FCSTD DOCUMENT  (FreeCAD 0.19R24291 (Git))
Label: curve_test
License: All rights reserved
LicenseURL: http://en.wikipedia.org/wiki/All_rights_reserved
objects: Sketcher::SketchObject×2, PartDesign::Body×1
note: 3 computed .brp shape members not serialized (recipe doc carries the construction recipe); baked Part::Feature solids carry a one-line shape summary decoded from their .brp

FEATURE [Sketcher::SketchObject] Sketch
  FullyConstrained = false
  MapMode = 5
  Placement = pos=(0,0,0) rot=(1,0,0;1.5708rad)
  Support = -> [XZ_Plane]
  sketch-geometry (15):
    g0-g4: Circle x5 (B-spline internal-alignment scaffolding for g5; pole/knot coordinates omitted)
    g5: BSplineCurve PolesCount=5 KnotsCount=3 Degree=3 IsPeriodic=0
    g6: GeomPoint X=-25.4415 Y=43.3775 Z=0
    g7: GeomPoint X=-23.7858 Y=19.2881 Z=0
    g8: GeomPoint X=-22.2406 Y=0 Z=0
    g9: Circle CenterX=-7.83243 CenterY=0 CenterZ=0 NormalX=0 NormalY=0 NormalZ=1 AngleXU=0 Radius=1
    g10: Circle CenterX=1.51501 CenterY=20.0593 CenterZ=0 NormalX=0 NormalY=0 NormalZ=1 AngleXU=0 Radius=1
    g11: Circle CenterX=-8.09944 CenterY=43.783 CenterZ=0 NormalX=0 NormalY=0 NormalZ=1 AngleXU=0 Radius=1
    g12: BSplineCurve PolesCount=3 KnotsCount=2 Degree=2 IsPeriodic=0
    g13: GeomPoint X=-7.83243 Y=0 Z=0
    g14: GeomPoint X=-8.09944 Y=43.783 Z=0
  constraints (16):
    c: Weight(g0) = 1
    c: Equal(g0, g1-g4) x4
    c: InternalAlignment(g0-g4 -> g5) x5
    c: InternalAlignment(g6,g5)
    c: InternalAlignment(g7,g5)
    c: InternalAlignment(g8,g5)
    c: PointOnObject(g5,g-1)
    c: PointOnObject(g12,g-1)
    c: Weight(g9) = 1
    c: Equal(g9,g10)
    c: Equal(g9,g11)
    c: InternalAlignment(g9,g12)
    c: InternalAlignment(g10,g12)
    c: InternalAlignment(g11,g12)
    c: InternalAlignment(g13,g12)
    c: InternalAlignment(g14,g12)
FEATURE [Sketcher::SketchObject] Sketch001
  ExternalGeometry = -> [Sketch]
  FullyConstrained = false
  MapMode = 5
  Support = -> [XY_Plane]
  sketch-geometry (2):
    g0: ArcOfCircle CenterX=-5.58317 CenterY=-1.4e-15 CenterZ=0 NormalX=0 NormalY=0 NormalZ=1 AngleXU=0 Radius=16.6574 StartAngle=2.8405 EndAngle=3.44268
    g1: LineSegment StartX=-7.83243 StartY=0 StartZ=0 EndX=-22.2406 EndY=0 EndZ=0
  constraints (4):
    c: Symmetric(g0,g0,g-1)
    c: PointOnObject(g1,g0)
    c: Coincident(g1,g-3)
    c: Coincident(g-4,g1)
FEATURE [PartDesign::Body] Body
  Group = -> [Sketch,Sketch001]
  Origin = -> Origin
